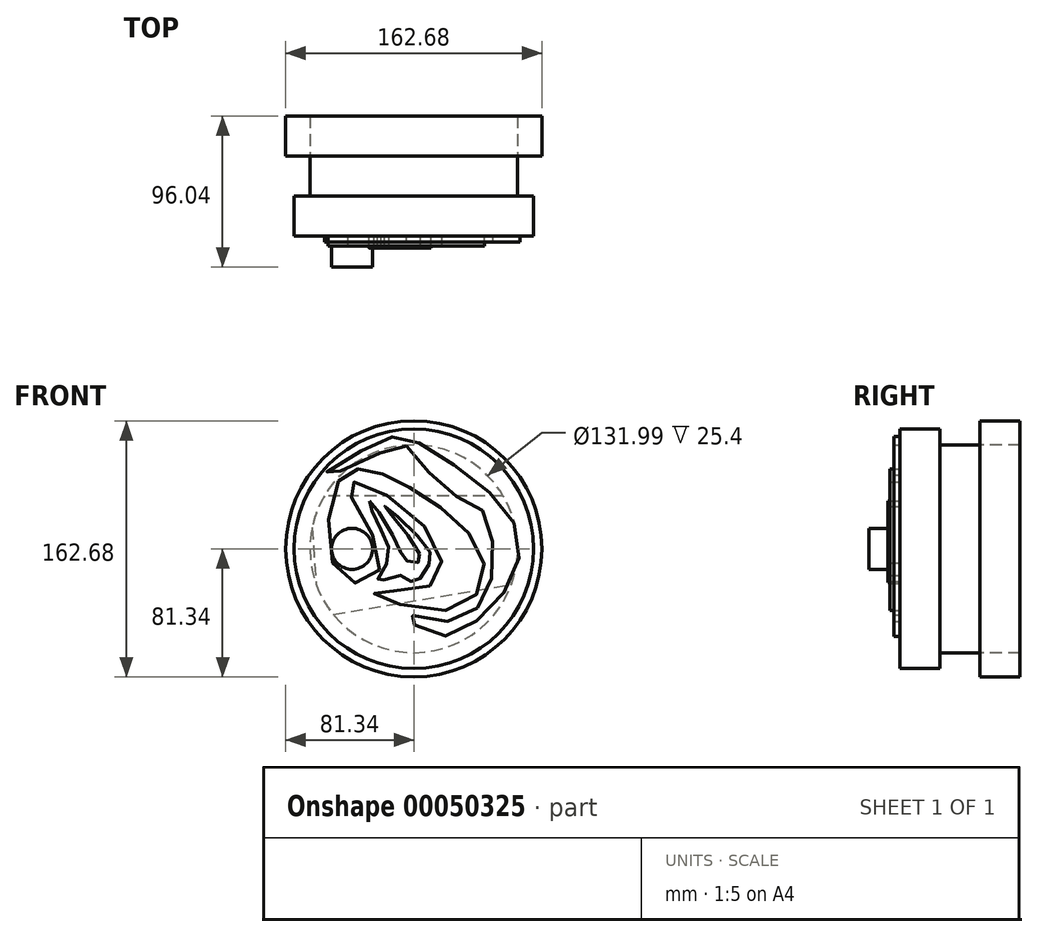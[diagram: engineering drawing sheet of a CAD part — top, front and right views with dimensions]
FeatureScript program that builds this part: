
annotation { "Feature Type Name" : "Feature", "Feature Type Description" : "" }
export const myFeature = defineFeature(function(context is Context, id is Id, definition is map)
    precondition{}
    {
        {
            var Q0;
            Q0=qCreatedBy(makeId("Front.planeOp"),FACE);
            var sketch = newSketch(context, id + "F0", { "sketchPlane" : qUnion([Q0])});
            skCircle(sketch, "E0", {"center": v(0, 0) * mm, "radius": 76.06 * mm});
            skSolve(sketch);
        }
        {
            var Q0;
            Q0=makeQuery(id+"F0.imprint","IMPRINT",FACE,{"disambiguationData":[TD([[makeQuery(id+"F0.imprint","IMPRINT",EDGE,{"derivedFrom":sQuery(id+"F0.wireOp",EDGE,"E0")}),1.0]])]});
            extrude(context, id + "F1", {"entities" : qUnion([Q0]), "depth" : 25.4 * mm});
        }
        {
            var Q0;
            Q0=makeQuery(id+"F1.opExtrude","CAP_FACE",FACE,{"disambiguationData":[OSD([sQuery(id+"F0.wireOp",EDGE,"E0")])],"isStart":false});
            var sketch = newSketch(context, id + "F2", { "sketchPlane" : qUnion([Q0])});
            skFitSpline(sketch, "E1", {"points": [v(-47.64, 43.02) * mm, v(-45.4, -18.64) * mm, v(-21.02, -10.5) * mm, v(-41.76, 40.5) * mm, v(4.2, 16.95) * mm, v(11.5, -22.84) * mm, v(-25.22, -27.88) * mm, v(25.22, -38.25) * mm, v(44, -6.03) * mm, v(5.6, 33.77) * mm, v(-28.59, 50.02) * mm, v(-47.64, 43.02) * mm]});
            skSolve(sketch);
        }
        {
            var Q0;
            Q0=makeQuery(id+"F2.imprint","IMPRINT",FACE,{"disambiguationData":[TD([[makeQuery(id+"F2.imprint","IMPRINT",EDGE,{"derivedFrom":sQuery(id+"F2.wireOp",EDGE,"E1")}),1.0]])]});
            extrude(context, id + "F3", {"entities" : qUnion([Q0]), "operationType" : NewBodyOperationType.ADD, "depth" : 6.35 * mm});
        }
        {
            var Q0;
            Q0=makeQuery(id+"F1.opExtrude","CAP_FACE",FACE,{"disambiguationData":[OSD([sQuery(id+"F0.wireOp",EDGE,"E0")])],"isStart":false});
            var sketch = newSketch(context, id + "F4", { "sketchPlane" : qUnion([Q0])});
            skFitSpline(sketch, "E2", {"points": [v(-4.48, 65.16) * mm, v(18.78, 38.25) * mm, v(42.32, 25.64) * mm, v(50.44, -2.38) * mm, v(43.16, -34.33) * mm, v(17.38, -46.1) * mm, v(-4.48, -42.46) * mm, v(10.93, -54.5) * mm, v(38.67, -46.66) * mm, v(64.74, -14.15) * mm, v(62.5, 18.64) * mm, v(27.18, 51.99) * mm, v(-7, 71.04) * mm, v(-27.18, 65.44) * mm, v(-56.6, 47.22) * mm, v(-28.3, 57.31) * mm, v(-4.48, 65.16) * mm]});
            skSolve(sketch);
        }
        {
            var Q0;
            Q0=makeQuery(id+"F4.imprint","IMPRINT",FACE,{"disambiguationData":[TD([[makeQuery(id+"F4.imprint","IMPRINT",EDGE,{"derivedFrom":sQuery(id+"F4.wireOp",EDGE,"E2")}),1.0]])]});
            extrude(context, id + "F5", {"entities" : qUnion([Q0]), "operationType" : NewBodyOperationType.ADD, "depth" : 3.8 * mm});
        }
        {
            var Q0;
            Q0=makeQuery(id+"F1.opExtrude","CAP_FACE",FACE,{"disambiguationData":[OSD([sQuery(id+"F0.wireOp",EDGE,"E0")])],"isStart":false});
            var sketch = newSketch(context, id + "F6", { "sketchPlane" : qUnion([Q0])});
            skFitSpline(sketch, "E3", {"points": [v(-28.02, 30.4) * mm, v(-22.7, 15.83) * mm, v(-16.25, -6.59) * mm, v(-22.98, -20.6) * mm, v(-7.57, -16.95) * mm, v(0, -21.44) * mm, v(9.8, -9.67) * mm, v(7.29, 2.66) * mm, v(-18.5, 27.04) * mm, v(0, 3.5) * mm, v(3.08, -8.55) * mm, v(-5.04, -7.15) * mm, v(-10.93, 3.78) * mm, v(-28.02, 30.4) * mm]});
            skSolve(sketch);
        }
        {
            var Q0;
            Q0=makeQuery(id+"F6.imprint","IMPRINT",FACE,{"disambiguationData":[TD([[makeQuery(id+"F6.imprint","IMPRINT",EDGE,{"derivedFrom":sQuery(id+"F6.wireOp",EDGE,"E3")}),1.0]])]});
            extrude(context, id + "F7", {"entities" : qUnion([Q0]), "operationType" : NewBodyOperationType.ADD, "depth" : 7.62 * mm});
        }
        {
            var Q0;
            Q0=makeQuery(id+"F3.opExtrude","CAP_FACE",FACE,{"disambiguationData":[OSD([sQuery(id+"F2.wireOp",EDGE,"E1")])],"isStart":false});
            var sketch = newSketch(context, id + "F8", { "sketchPlane" : qUnion([Q0])});
            skCircle(sketch, "E4", {"center": v(-39.23, 0) * mm, "radius": 13.03 * mm});
            skSolve(sketch);
        }
        {
            var Q0;
            Q0=makeQuery(id+"F8.imprint","IMPRINT",FACE,{"disambiguationData":[TD([[makeQuery(id+"F8.imprint","IMPRINT",EDGE,{"derivedFrom":sQuery(id+"F8.wireOp",EDGE,"E4")}),1.0]])]});
            extrude(context, id + "F9", {"entities" : qUnion([Q0]), "operationType" : NewBodyOperationType.ADD, "depth" : 13.46 * mm});
        }
        {
            var Q0;
            Q0=makeQuery(id+"F1.opExtrude","CAP_FACE",FACE,{"disambiguationData":[OSD([sQuery(id+"F0.wireOp",EDGE,"E0")])],"isStart":true});
            var sketch = newSketch(context, id + "F10", { "sketchPlane" : qUnion([Q0])});
            skCircle(sketch, "E5", {"center": v(0, 0) * mm, "radius": 66 * mm});
            skSolve(sketch);
        }
        {
            var Q0;
            Q0=makeQuery(id+"F10.imprint","IMPRINT",FACE,{"disambiguationData":[TD([[makeQuery(id+"F10.imprint","IMPRINT",EDGE,{"derivedFrom":sQuery(id+"F10.wireOp",EDGE,"E5")}),1.0]])]});
            extrude(context, id + "F11", {"entities" : qUnion([Q0]), "operationType" : NewBodyOperationType.ADD, "depth" : 25.4 * mm});
        }
        {
            var Q0;
            Q0=makeQuery(id+"F11.opExtrude","CAP_FACE",FACE,{"disambiguationData":[OSD([sQuery(id+"F10.wireOp",EDGE,"E5")])],"isStart":false});
            var sketch = newSketch(context, id + "F12", { "sketchPlane" : qUnion([Q0])});
            skCircle(sketch, "E6", {"center": v(0, 0) * mm, "radius": 81.34 * mm});
            skSolve(sketch);
        }
        {
            var Q0;
            Q0=makeQuery(id+"F12.imprint","IMPRINT",FACE,{"disambiguationData":[TD([[makeQuery(id+"F12.imprint","IMPRINT",EDGE,{"derivedFrom":sQuery(id+"F12.wireOp",EDGE,"E6")}),1.0]])]});
            extrude(context, id + "F13", {"entities" : qUnion([Q0]), "depth" : 25.4 * mm});
        }
        {
            var Q0;
            Q0=makeQuery(id+"F13.opExtrude","CAP_FACE",FACE,{"disambiguationData":[OSD([sQuery(id+"F10.wireOp",EDGE,"E5"),sQuery(id+"F12.wireOp",EDGE,"E6")])],"isStart":false});
            var sketch = newSketch(context, id + "F14", { "sketchPlane" : qUnion([Q0])});
            skLineSegment(sketch, "E7", {"start": v(-68.93, 33.65) * mm, "end": v(66.03, 33.65) * mm});
            skLineSegment(sketch, "E8", {"start": v(66.03, 33.65) * mm, "end": v(60.53, -43.23) * mm});
            skLineSegment(sketch, "E9", {"start": v(60.53, -43.23) * mm, "end": v(-73.58, -20.8) * mm});
            skLineSegment(sketch, "E10", {"start": v(-73.58, -20.8) * mm, "end": v(-68.93, 33.65) * mm});
            skSolve(sketch);
        }
        {
            var Q0;
            {var subQ1=makeQuery(id+"F13.opExtrude","CAP_EDGE",EDGE,{"disambiguationData":[OSD([sQuery(id+"F10.wireOp",EDGE,"E5")])],"isStart":false});var subQ4=sQuery(id+"F14.wireOp",EDGE,"E7");var subQ8=makeQuery(id+"F14.imprint","INTERSECT",VERTEX,{"disambiguationData":[OD(0.0)],"derivedFrom":[subQ1,subQ4]});Q0=makeQuery(id+"F14.imprint","IMPRINT",FACE,{"disambiguationData":[TD([[makeQuery(id+"F14.imprint","IMPRINT",EDGE,{"disambiguationData":[TD([[subQ8,-1.0]])],"derivedFrom":subQ4}),-1.0]])]});}
            extrude(context, id + "F15", {"entities" : qUnion([Q0]), "depth" : 0.03 * mm});
        }
    });
